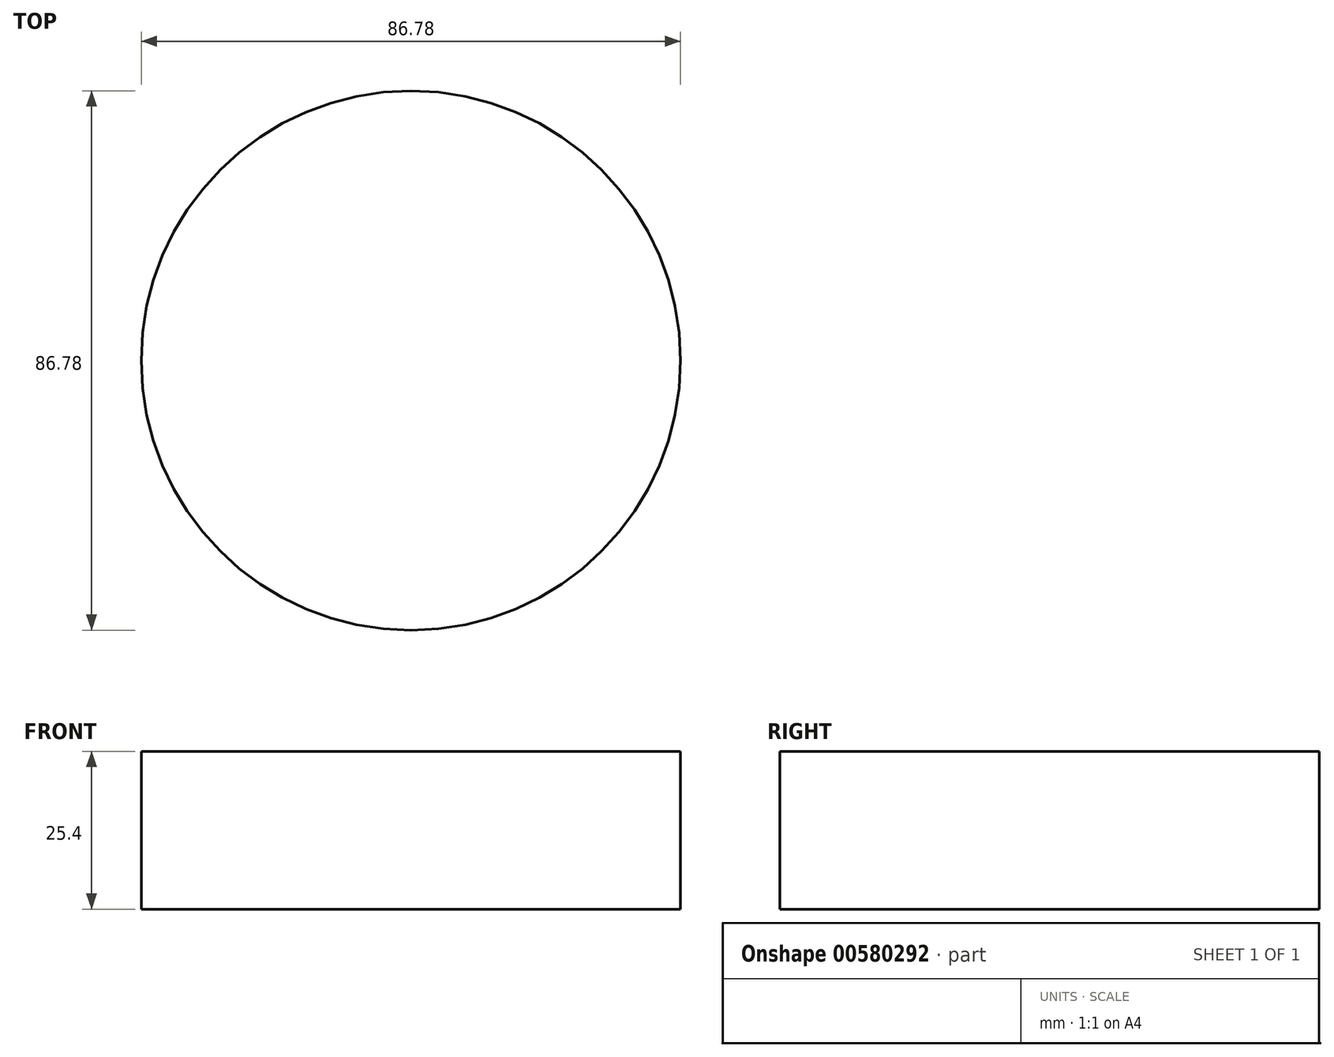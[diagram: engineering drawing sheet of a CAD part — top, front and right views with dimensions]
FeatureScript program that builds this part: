
annotation { "Feature Type Name" : "Feature", "Feature Type Description" : "" }
export const myFeature = defineFeature(function(context is Context, id is Id, definition is map)
    precondition{}
    {
        {
            var Q0;
            Q0=qCreatedBy(makeId("Top.planeOp"),FACE);
            var sketch = newSketch(context, id + "F0", { "sketchPlane" : qUnion([Q0])});
            skCircle(sketch, "E0", {"center": v(0, 0) * mm, "radius": 43.4 * mm});
            skCircle(sketch, "E1", {"center": v(0, 0) * mm, "radius": 20.46 * mm});
            skSolve(sketch);
        }
        {
            var Q0;
            Q0=makeQuery(id+"F0.imprint","IMPRINT",FACE,{"disambiguationData":[TD([[makeQuery(id+"F0.imprint","IMPRINT",EDGE,{"derivedFrom":sQuery(id+"F0.wireOp",EDGE,"E0")}),1.0]])]});
            var Q1;
            Q1=makeQuery(id+"F0.imprint","IMPRINT",FACE,{"disambiguationData":[TD([[makeQuery(id+"F0.imprint","IMPRINT",EDGE,{"derivedFrom":sQuery(id+"F0.wireOp",EDGE,"E1")}),1.0]])]});
            extrude(context, id + "F1", {"entities" : qUnion([Q0, Q1]), "depth" : 25.4 * mm, "offsetDistance" : 25.4 * mm});
        }
    });
